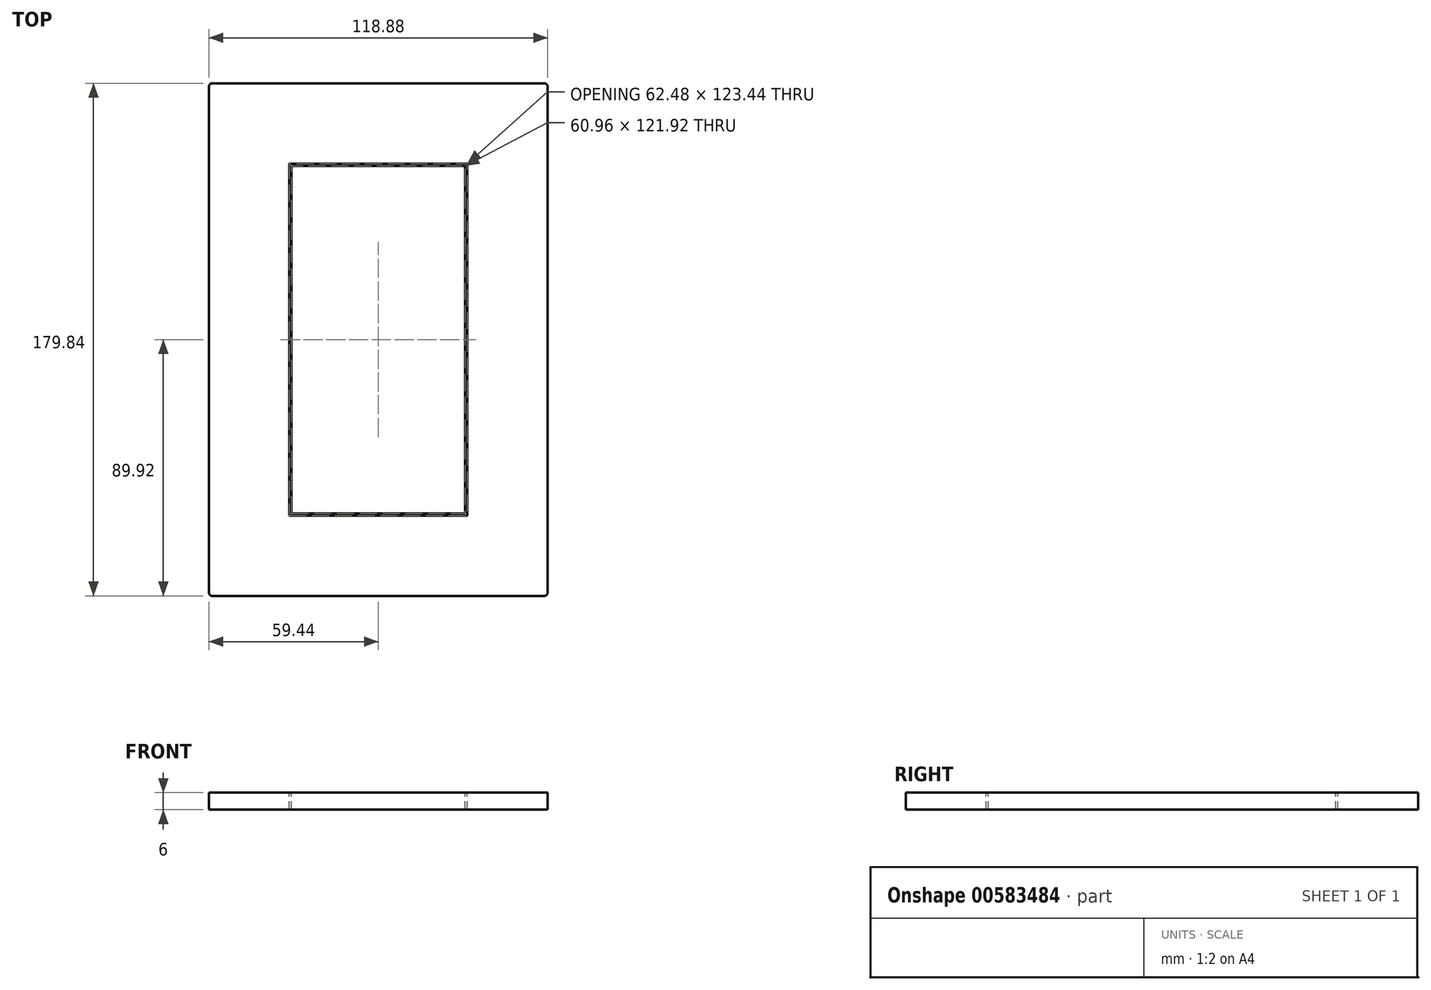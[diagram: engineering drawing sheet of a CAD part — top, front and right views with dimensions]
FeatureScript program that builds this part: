
annotation { "Feature Type Name" : "Feature", "Feature Type Description" : "" }
export const myFeature = defineFeature(function(context is Context, id is Id, definition is map)
    precondition{}
    {
        {
            assignVariable(context, id + "F0", {"name" : "Tongue", "anyValue" : 2.4});
        }
        {
            assignVariable(context, id + "F1", {"name" : "WindingWidth", "anyValue" : 6});
        }
        {
            assignVariable(context, id + "F2", {"name" : "CoilBuild", "anyValue" : 0.47 * getVariable(context, 'Tongue')});
        }
        {
            assignVariable(context, id + "F3", {"name" : "CoilForm", "anyValue" : 0.03});
        }
        {
            var Q0;
            Q0=qCreatedBy(makeId("Top.planeOp"),FACE);
            var sketch = newSketch(context, id + "F4", { "sketchPlane" : qUnion([Q0])});
            skLineSegment(sketch, "E0.bottom", {"start": v(-59.44, -89.92) * mm, "end": v(59.44, -89.92) * mm});
            skLineSegment(sketch, "E0.top", {"start": v(-59.44, 89.92) * mm, "end": v(59.44, 89.92) * mm});
            skLineSegment(sketch, "E0.left", {"start": v(-59.44, -89.92) * mm, "end": v(-59.44, 89.92) * mm});
            skLineSegment(sketch, "E0.right", {"start": v(59.44, -89.92) * mm, "end": v(59.44, 89.92) * mm});
            skPoint(sketch, "E0.middle", {"position": v(0, 0) * mm});
            skSolve(sketch);
        }
        {
            var Q0;
            Q0=qSketchRegion(id+"F4",true);
            extrude(context, id + "F5", {"entities" : qUnion([Q0]), "oppositeDirection" : true, "depth" : (getVariable(context, 'WindingWidth')) * mm});
        }
        {
            var Q0;
            Q0=makeQuery(id+"F5.opExtrude","SWEPT_EDGE",EDGE,{"disambiguationData":[OSD([sQuery(id+"F4.wireOp",EDGE,"E0.top"),sQuery(id+"F4.wireOp",EDGE,"E0.left")])]});
            var Q1;
            Q1=makeQuery(id+"F5.opExtrude","SWEPT_EDGE",EDGE,{"disambiguationData":[OSD([sQuery(id+"F4.wireOp",EDGE,"E0.top"),sQuery(id+"F4.wireOp",EDGE,"E0.right")])]});
            var Q2;
            Q2=makeQuery(id+"F5.opExtrude","SWEPT_EDGE",EDGE,{"disambiguationData":[OSD([sQuery(id+"F4.wireOp",EDGE,"E0.bottom"),sQuery(id+"F4.wireOp",EDGE,"E0.right")])]});
            var Q3;
            Q3=makeQuery(id+"F5.opExtrude","SWEPT_EDGE",EDGE,{"disambiguationData":[OSD([sQuery(id+"F4.wireOp",EDGE,"E0.bottom"),sQuery(id+"F4.wireOp",EDGE,"E0.left")])]});
            fillet(context, id + "F6", {"entities" : qUnion([Q0, Q1, Q2, Q3]), "radius" : (getVariable(context, 'CoilBuild')) * mm, "tangentPropagation" : true, "allowEdgeOverflow" : false});
        }
        {
            var Q0;
            Q0=makeQuery(id+"F5.opExtrude","CAP_FACE",FACE,{"disambiguationData":[OSD([sQuery(id+"F4.wireOp",EDGE,"E0.bottom"),sQuery(id+"F4.wireOp",EDGE,"E0.top"),sQuery(id+"F4.wireOp",EDGE,"E0.left"),sQuery(id+"F4.wireOp",EDGE,"E0.right")])],"isStart":true});
            var sketch = newSketch(context, id + "F7", { "sketchPlane" : qUnion([Q0])});
            skLineSegment(sketch, "E1.bottom", {"start": v(-31.24, -61.72) * mm, "end": v(31.24, -61.72) * mm});
            skLineSegment(sketch, "E1.top", {"start": v(-31.24, 61.72) * mm, "end": v(31.24, 61.72) * mm});
            skLineSegment(sketch, "E1.left", {"start": v(-31.24, -61.72) * mm, "end": v(-31.24, 61.72) * mm});
            skLineSegment(sketch, "E1.right", {"start": v(31.24, -61.72) * mm, "end": v(31.24, 61.72) * mm});
            skPoint(sketch, "E1.middle", {"position": v(0, 0) * mm});
            skSolve(sketch);
        }
        {
            var Q0;
            Q0=qSketchRegion(id+"F7",true);
            extrude(context, id + "F8", {"entities" : qUnion([Q0]), "operationType" : NewBodyOperationType.REMOVE, "oppositeDirection" : true, "depth" : (getVariable(context, 'WindingWidth')) * mm});
        }
        {
            var Q0;
            Q0=makeQuery(id+"F5.opExtrude","CAP_FACE",FACE,{"disambiguationData":[OSD([sQuery(id+"F4.wireOp",EDGE,"E0.bottom"),sQuery(id+"F4.wireOp",EDGE,"E0.top"),sQuery(id+"F4.wireOp",EDGE,"E0.left"),sQuery(id+"F4.wireOp",EDGE,"E0.right")])],"isStart":true});
            var sketch = newSketch(context, id + "F9", { "sketchPlane" : qUnion([Q0])});
            skLineSegment(sketch, "E2.bottom", {"start": v(-31.24, -61.72) * mm, "end": v(31.24, -61.72) * mm});
            skLineSegment(sketch, "E2.top", {"start": v(-31.24, 61.72) * mm, "end": v(31.24, 61.72) * mm});
            skLineSegment(sketch, "E2.left", {"start": v(-31.24, -61.72) * mm, "end": v(-31.24, 61.72) * mm});
            skLineSegment(sketch, "E2.right", {"start": v(31.24, -61.72) * mm, "end": v(31.24, 61.72) * mm});
            skPoint(sketch, "E2.middle", {"position": v(0, 0) * mm});
            skSolve(sketch);
        }
        {
            var Q0;
            Q0=qSketchRegion(id+"F9",true);
            extrude(context, id + "F10", {"entities" : qUnion([Q0]), "oppositeDirection" : true, "depth" : (getVariable(context, 'WindingWidth')) * mm});
        }
        {
            var Q0;
            Q0=makeQuery(id+"F10.opExtrude","CAP_FACE",FACE,{"disambiguationData":[OSD([sQuery(id+"F9.wireOp",EDGE,"E2.bottom"),sQuery(id+"F9.wireOp",EDGE,"E2.top"),sQuery(id+"F9.wireOp",EDGE,"E2.left"),sQuery(id+"F9.wireOp",EDGE,"E2.right")])],"isStart":true});
            var sketch = newSketch(context, id + "F11", { "sketchPlane" : qUnion([Q0])});
            skLineSegment(sketch, "E3.bottom", {"start": v(-30.48, 60.96) * mm, "end": v(30.48, 60.96) * mm});
            skLineSegment(sketch, "E3.top", {"start": v(-30.48, -60.96) * mm, "end": v(30.48, -60.96) * mm});
            skLineSegment(sketch, "E3.left", {"start": v(-30.48, 60.96) * mm, "end": v(-30.48, -60.96) * mm});
            skLineSegment(sketch, "E3.right", {"start": v(30.48, 60.96) * mm, "end": v(30.48, -60.96) * mm});
            skPoint(sketch, "E3.middle", {"position": v(0, 0) * mm});
            skSolve(sketch);
        }
        {
            var Q0;
            Q0=qSketchRegion(id+"F11",true);
            extrude(context, id + "F12", {"entities" : qUnion([Q0]), "operationType" : NewBodyOperationType.REMOVE, "oppositeDirection" : true, "depth" : (getVariable(context, 'WindingWidth')) * mm});
        }
        {
            var Q0;
            Q0=makeQuery(id+"F10.opExtrude","SWEPT_EDGE",EDGE,{"disambiguationData":[OSD([sQuery(id+"F9.wireOp",EDGE,"E2.top"),sQuery(id+"F9.wireOp",EDGE,"E2.left")])]});
            var Q1;
            Q1=makeQuery(id+"F10.opExtrude","SWEPT_EDGE",EDGE,{"disambiguationData":[OSD([sQuery(id+"F9.wireOp",EDGE,"E2.top"),sQuery(id+"F9.wireOp",EDGE,"E2.right")])]});
            var Q2;
            Q2=makeQuery(id+"F10.opExtrude","SWEPT_EDGE",EDGE,{"disambiguationData":[OSD([sQuery(id+"F9.wireOp",EDGE,"E2.bottom"),sQuery(id+"F9.wireOp",EDGE,"E2.right")])]});
            var Q3;
            Q3=makeQuery(id+"F10.opExtrude","SWEPT_EDGE",EDGE,{"disambiguationData":[OSD([sQuery(id+"F9.wireOp",EDGE,"E2.bottom"),sQuery(id+"F9.wireOp",EDGE,"E2.left")])]});
            fillet(context, id + "F13", {"entities" : qUnion([Q0, Q1, Q2, Q3]), "radius" : (getVariable(context, 'CoilForm')) * mm, "allowEdgeOverflow" : false});
        }
        {
            var Q0;
            Q0=makeQuery(id+"F8.boolean.opBoolean","COPY",EDGE,{"derivedFrom":makeQuery(id+"F8.opExtrude","SWEPT_EDGE",EDGE,{"disambiguationData":[OSD([sQuery(id+"F7.wireOp",EDGE,"E1.top"),sQuery(id+"F7.wireOp",EDGE,"E1.left")])]})});
            var Q1;
            Q1=makeQuery(id+"F8.boolean.opBoolean","COPY",EDGE,{"derivedFrom":makeQuery(id+"F8.opExtrude","SWEPT_EDGE",EDGE,{"disambiguationData":[OSD([sQuery(id+"F7.wireOp",EDGE,"E1.bottom"),sQuery(id+"F7.wireOp",EDGE,"E1.left")])]})});
            var Q2;
            Q2=makeQuery(id+"F8.boolean.opBoolean","COPY",EDGE,{"derivedFrom":makeQuery(id+"F8.opExtrude","SWEPT_EDGE",EDGE,{"disambiguationData":[OSD([sQuery(id+"F7.wireOp",EDGE,"E1.bottom"),sQuery(id+"F7.wireOp",EDGE,"E1.right")])]})});
            var Q3;
            Q3=makeQuery(id+"F8.boolean.opBoolean","COPY",EDGE,{"derivedFrom":makeQuery(id+"F8.opExtrude","SWEPT_EDGE",EDGE,{"disambiguationData":[OSD([sQuery(id+"F7.wireOp",EDGE,"E1.top"),sQuery(id+"F7.wireOp",EDGE,"E1.right")])]})});
            fillet(context, id + "F14", {"entities" : qUnion([Q0, Q1, Q2, Q3]), "radius" : (getVariable(context, 'CoilForm')) * mm, "tangentPropagation" : true, "allowEdgeOverflow" : false});
        }
    });
